# Revit family: 873-00-001-DN1100-1200
name_source: partatom
category: Generic Models
units: mm (PartAtom-declared; Revit-internal decimal feet)

## family parameters
Always vertical = Yes
Can host rebar = No
Cut with Voids When Loaded = No
Part Type = Normal
Room Calculation Point = No
Round Connector Dimension = Use Diameter
Shared = No
Work Plane-Based = No

## types (4) — shared parameters
873-1100-00-041000 = DN1100_PN10
873-1100-00-141000 = DN1100_PN16
873-1200-00-041000 = DN1200_PN10
873-1200-00-141000 = DN1200_PN16
Angle = 22.50°
Body_Wallthicknss = 10 mm  [stored 0.0328084 ft]
Description_ = AVK DISMANTLING JOINT
Flange_thickness = 20 mm  [stored 0.0656168 ft]
Search_table = 873-00-001-DN1100-1200
URL product pages = https://www.avkvalves.com

## per-type parameters (varying)
| type | A | DN | Id(Radius) | L | T | d1 | d2 |
| DN1100_PN10 | 320 mm  [stored 1.04987 ft] | 1100 mm  [stored 3.60892 ft] | 550 mm | 480 mm  [stored 1.5748 ft] | 33 mm  [stored 0.108268 ft] | 1270 mm  [stored 4.16667 ft] | 670 mm  [stored 2.19816 ft] |
| DN1100_PN16 | 320 mm  [stored 1.04987 ft] | 1100 mm  [stored 3.60892 ft] | 550 mm | 560 mm  [stored 1.83727 ft] | 39 mm  [stored 0.127953 ft] | 1270 mm  [stored 4.16667 ft] | 678 mm |
| DN1200_PN10 | 345 mm  [stored 1.13189 ft] | 1200 mm  [stored 3.93701 ft] | 600 mm | 580 mm  [stored 1.90289 ft] | 36 mm  [stored 0.11811 ft] | 1380 mm  [stored 4.52756 ft] | 728 mm |
| DN1200_PN16 | 345 mm  [stored 1.13189 ft] | 1200 mm  [stored 3.93701 ft] | 600 mm | 620 mm  [stored 2.03412 ft] | 45 mm  [stored 0.147638 ft] | 1390 mm  [stored 4.56037 ft] | 743 mm |

note: [stored X ft] marks values corroborated as IEEE doubles in the binary element streams (Revit-internal decimal feet)

## geometry (parser evidence)
native form markers: Sweep x4
no freeform markers — native parametric forms only
